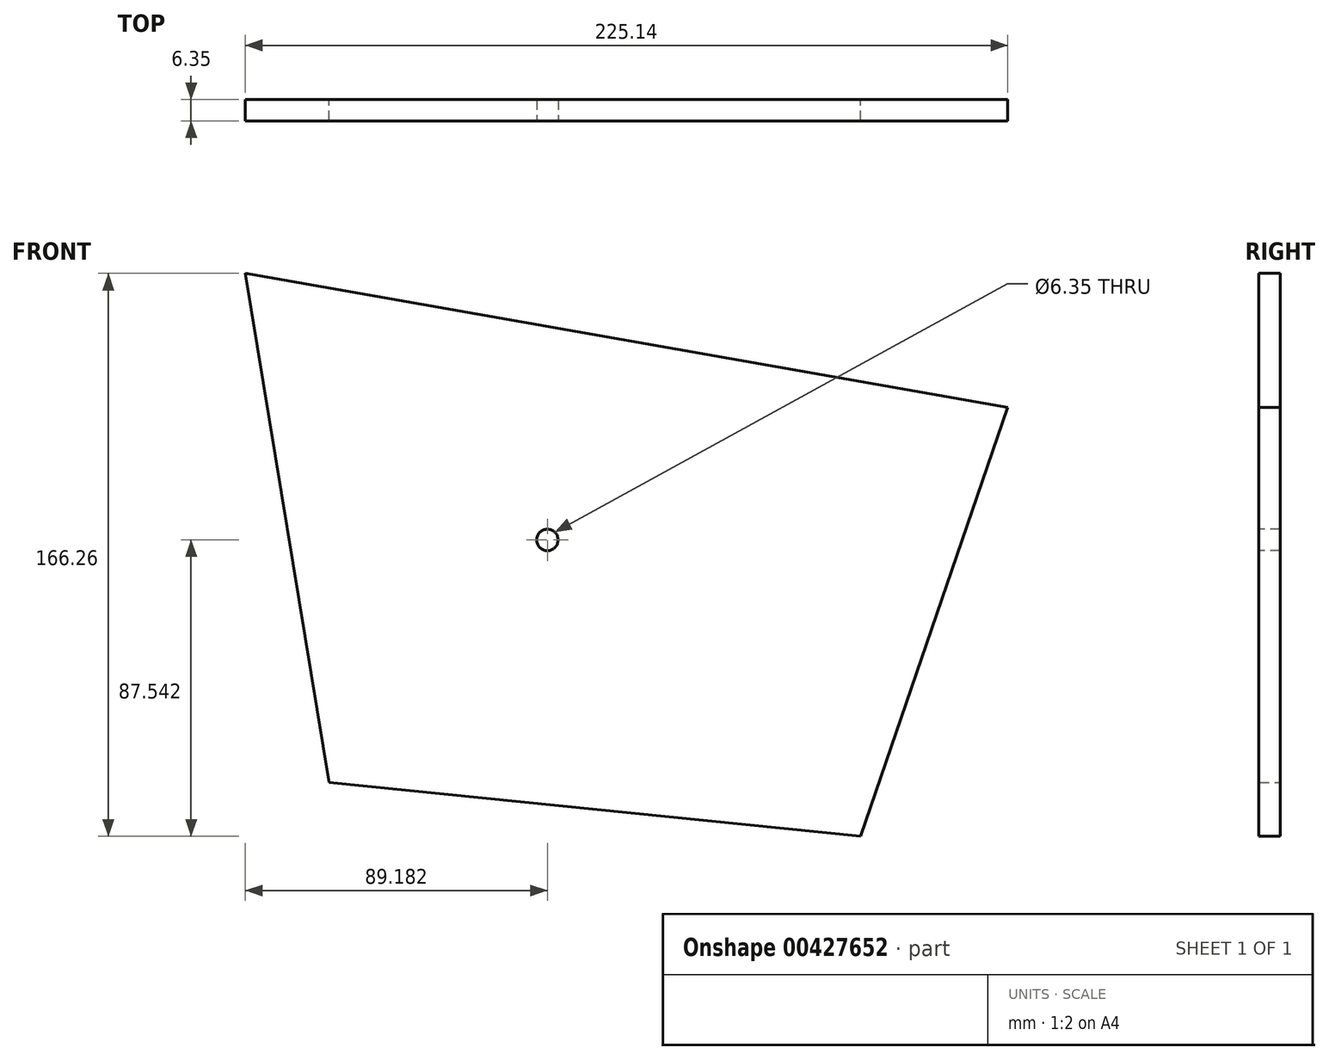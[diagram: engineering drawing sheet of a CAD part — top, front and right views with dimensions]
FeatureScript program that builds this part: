
annotation { "Feature Type Name" : "Feature", "Feature Type Description" : "" }
export const myFeature = defineFeature(function(context is Context, id is Id, definition is map)
    precondition{}
    {
        {
            var Q0;
            Q0=qCreatedBy(makeId("Front.planeOp"),FACE);
            var sketch = newSketch(context, id + "F0", { "sketchPlane" : qUnion([Q0])});
            skLineSegment(sketch, "E0", {"start": v(-157.36, 150.38) * mm, "end": v(-132.65, 0) * mm});
            skLineSegment(sketch, "E1", {"start": v(-132.65, 0) * mm, "end": v(24.29, -15.88) * mm});
            skLineSegment(sketch, "E2", {"start": v(24.29, -15.88) * mm, "end": v(67.78, 110.75) * mm});
            skLineSegment(sketch, "E3", {"start": v(67.78, 110.75) * mm, "end": v(-157.36, 150.38) * mm});
            skSolve(sketch);
        }
        {
            var Q0;
            Q0 = qSketchRegion(id + "F0", true);
            extrude(context, id + "F1", {"entities" : qUnion([Q0]), "depth" : 6.35 * mm});
        }
        {
            var Q0;
            Q0=makeQuery(id+"F1.opExtrude","CAP_FACE",FACE,{"disambiguationData":[OSD([sQuery(id+"F0.wireOp",EDGE,"E0"),sQuery(id+"F0.wireOp",EDGE,"E1"),sQuery(id+"F0.wireOp",EDGE,"E2"),sQuery(id+"F0.wireOp",EDGE,"E3")])],"isStart":false});
            var sketch = newSketch(context, id + "F2", { "sketchPlane" : qUnion([Q0])});
            skCircle(sketch, "E4", {"center": v(-68.18, 71.66) * mm, "radius": 1.59 * mm});
            skSolve(sketch);
        }
        {
            var Q0;
            Q0=sQuery(id+"F2.wireOp",VERTEX,"E4.center");
            var Q1;
            Q1=makeQuery(id+"F1.opExtrude","SWEPT_BODY",BODY,{"disambiguationData":[OSD([sQuery(id+"F0.wireOp",EDGE,"E0"),sQuery(id+"F0.wireOp",EDGE,"E1"),sQuery(id+"F0.wireOp",EDGE,"E2"),sQuery(id+"F0.wireOp",EDGE,"E3")])]});
            hole(context, id + "F3", {"style" : HoleStyle.SIMPLE, "endStyle" : HoleEndStyle.THROUGH, "holeDiameter" : 6.35 * mm, "isTappedThrough" : true, "tappedDepth" : 12.7 * mm, "tapClearance" : 3, "locations" : qUnion([Q0]), "scope" : qUnion([Q1])});
        }
    });
